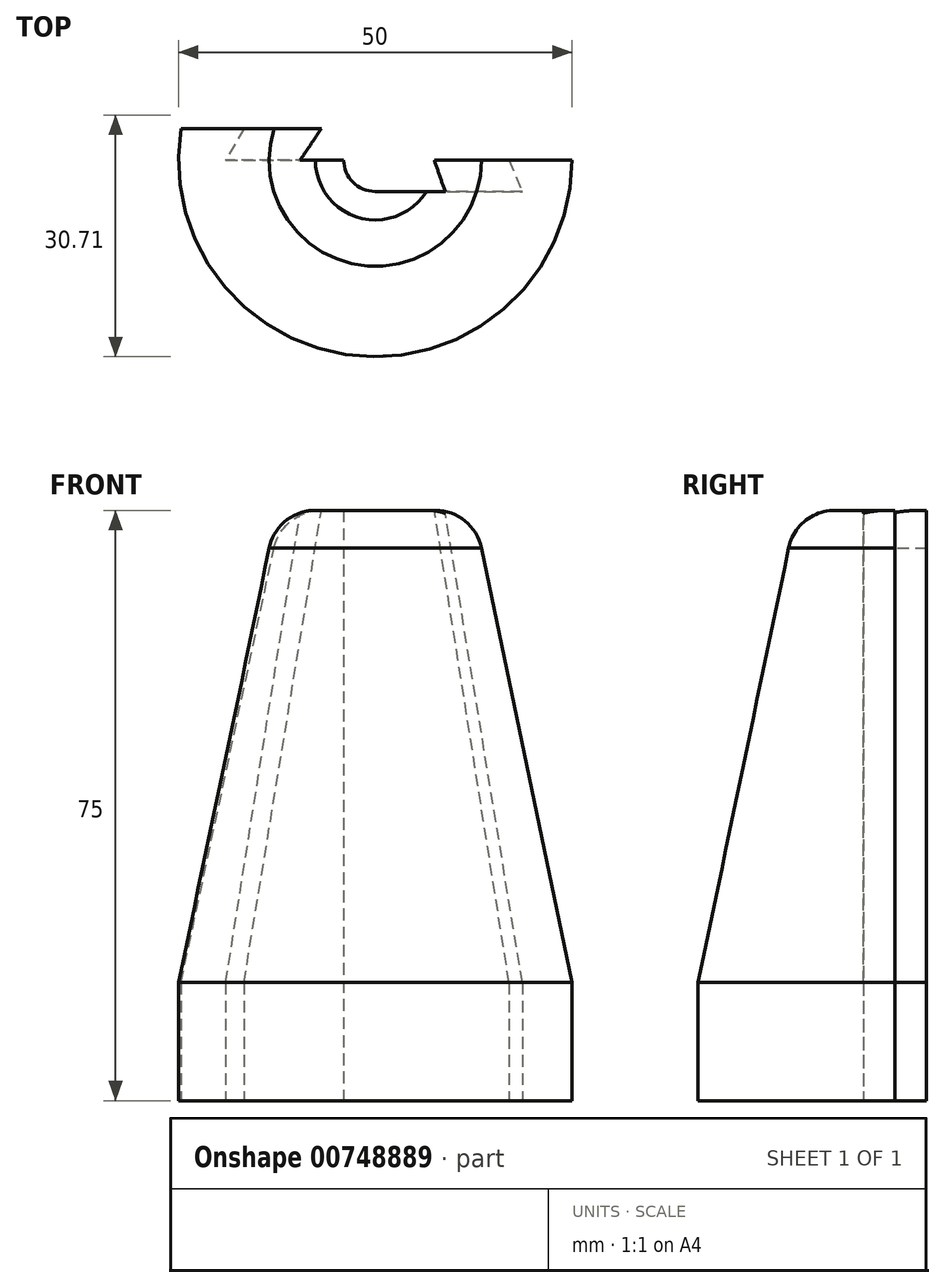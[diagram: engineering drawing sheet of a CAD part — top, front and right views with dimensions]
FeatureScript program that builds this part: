
annotation { "Feature Type Name" : "Feature", "Feature Type Description" : "" }
export const myFeature = defineFeature(function(context is Context, id is Id, definition is map)
    precondition{}
    {
        {
            var Q0;
            Q0=qCreatedBy(makeId("Top.planeOp"),FACE);
            var sketch = newSketch(context, id + "F0", { "sketchPlane" : qUnion([Q0])});
            skArc(sketch, "E0", {"start": v(-4, 0) * mm, "mid": v(-2.83, -2.83) * mm, "end": v(0, -4) * mm});
            skLineSegment(sketch, "E1", {"start": v(0, -4) * mm, "end": v(18.68, -4) * mm});
            skArc(sketch, "E2", {"start": v(-24.68, 4) * mm, "mid": v(-2, -24.92) * mm, "end": v(25, 0) * mm});
            skLineSegment(sketch, "E3", {"start": v(-24.68, 4) * mm, "end": v(-16.68, 4) * mm});
            skLineSegment(sketch, "E4", {"start": v(17, 0) * mm, "end": v(25, 0) * mm});
            skLineSegment(sketch, "E5", {"start": v(-16.68, 4) * mm, "end": v(-19, 0) * mm});
            skLineSegment(sketch, "E6", {"start": v(-4, 0) * mm, "end": v(-19, 0) * mm});
            skLineSegment(sketch, "E7", {"start": v(17, 0) * mm, "end": v(18.68, -4) * mm});
            skPoint(sketch, "E8.orphan", {"position": v(24.68, -4) * mm});
            skSolve(sketch);
        }
        {
            var Q0;
            Q0 = qSketchRegion(id + "F0", true);
            extrude(context, id + "F1", {"entities" : qUnion([Q0]), "depth" : 15 * mm, "offsetDistance" : 25 * mm});
        }
        {
            var Q0;
            Q0=makeQuery(id+"F1.opExtrude","CAP_FACE",FACE,{"disambiguationData":[OSD([sQuery(id+"F0.wireOp",EDGE,"E0"),sQuery(id+"F0.wireOp",EDGE,"E1"),sQuery(id+"F0.wireOp",EDGE,"E2"),sQuery(id+"F0.wireOp",EDGE,"E3"),sQuery(id+"F0.wireOp",EDGE,"E4"),sQuery(id+"F0.wireOp",EDGE,"E5"),sQuery(id+"F0.wireOp",EDGE,"E6"),sQuery(id+"F0.wireOp",EDGE,"E7")])],"isStart":false});
            cPlane(context, id + "F2", {"entities" : qUnion([Q0]), "cplaneType" : CPlaneType.OFFSET, "offset" : 60 * mm, "width" : 150 * mm, "height" : 150 * mm});
        }
        {
            var Q0;
            Q0=qCreatedBy(id+"F2.planeOp",FACE);
            var sketch = newSketch(context, id + "F3", { "sketchPlane" : qUnion([Q0])});
            skArc(sketch, "E9", {"start": v(-4, 0) * mm, "mid": v(-2.83, -2.83) * mm, "end": v(0, -4) * mm});
            skArc(sketch, "E10", {"start": v(-11.84, 4) * mm, "mid": v(-2.03, -12.33) * mm, "end": v(12.5, 0) * mm});
            skLineSegment(sketch, "E11", {"start": v(-4, 0) * mm, "end": v(-9.5, 0) * mm});
            skLineSegment(sketch, "E12", {"start": v(-11.84, 4) * mm, "end": v(-6.84, 4) * mm});
            skLineSegment(sketch, "E13", {"start": v(-6.84, 4) * mm, "end": v(-9.5, 0) * mm});
            skLineSegment(sketch, "E14", {"start": v(8.84, -4) * mm, "end": v(7.5, 0) * mm});
            skLineSegment(sketch, "E15", {"start": v(7.5, 0) * mm, "end": v(12.5, 0) * mm});
            skPoint(sketch, "E16.orphan", {"position": v(-12.5, 0) * mm});
            skPoint(sketch, "E17.orphan", {"position": v(11.84, -4) * mm});
            skLineSegment(sketch, "E18", {"start": v(-9.5, 0) * mm, "end": v(-4, 0) * mm});
            skLineSegment(sketch, "E19", {"start": v(0, -4) * mm, "end": v(8.84, -4) * mm});
            skSolve(sketch);
        }
        {
            var Q1;
            Q1=makeQuery(id+"F1.opExtrude","CAP_FACE",FACE,{"disambiguationData":[OSD([sQuery(id+"F0.wireOp",EDGE,"E0"),sQuery(id+"F0.wireOp",EDGE,"E1"),sQuery(id+"F0.wireOp",EDGE,"E2"),sQuery(id+"F0.wireOp",EDGE,"E3"),sQuery(id+"F0.wireOp",EDGE,"E4"),sQuery(id+"F0.wireOp",EDGE,"E5"),sQuery(id+"F0.wireOp",EDGE,"E6"),sQuery(id+"F0.wireOp",EDGE,"E7")])],"isStart":false});
            var Q2;
            Q2=makeQuery(id+"F3.imprint","IMPRINT",FACE,{"disambiguationData":[TD([[makeQuery(id+"F3.imprint","IMPRINT",EDGE,{"derivedFrom":sQuery(id+"F3.wireOp",EDGE,"E9")}),-1.0]])]});
            loft(context, id + "F4", {"operationType" : NewBodyOperationType.ADD, "sheetProfilesArray" : [{ "sheetProfileEntities" : qUnion([Q1]) }, { "sheetProfileEntities" : qUnion([Q2]) }]});
        }
        {
            var Q0;
            Q0=makeQuery(id+"F4.opLoft","MID_CAP_EDGE",EDGE,{"disambiguationData":[OSD([sQuery(id+"F3.wireOp",EDGE,"E10"),sQuery(id+"F3.wireOp",EDGE,"E12"),sQuery(id+"F3.wireOp",EDGE,"E15")])],"capPos":1.0});
            fillet(context, id + "F5", {"entities" : qUnion([Q0]), "radius" : 6 * mm, "tangentPropagation" : true, "allowEdgeOverflow" : false});
        }
    });
